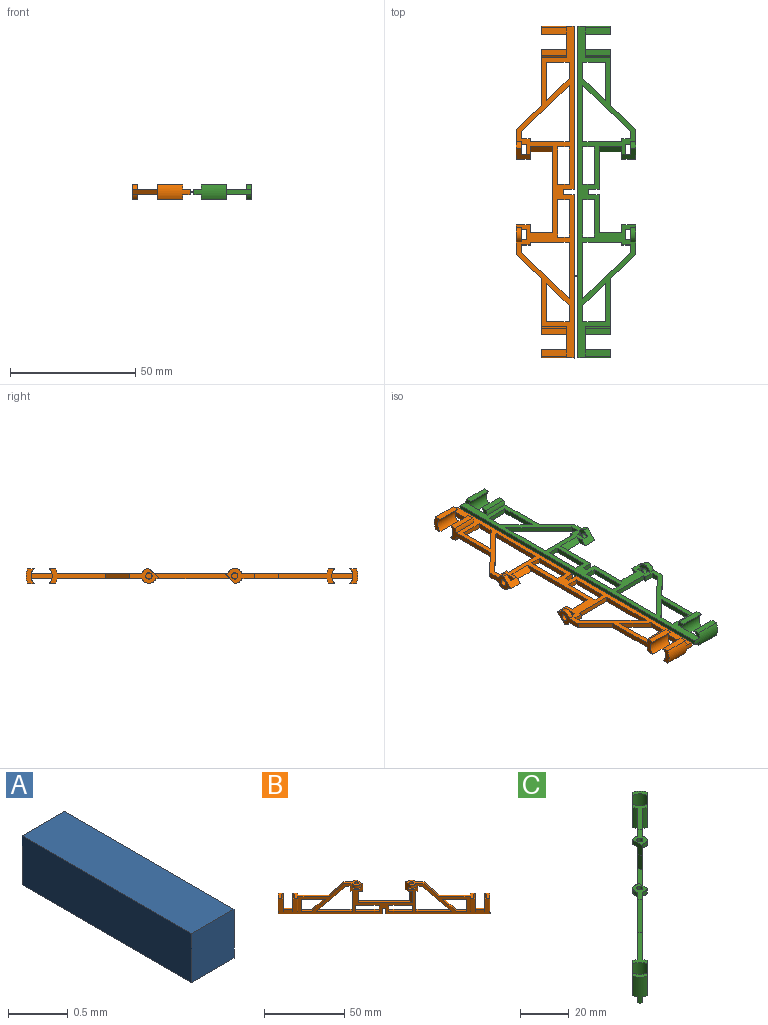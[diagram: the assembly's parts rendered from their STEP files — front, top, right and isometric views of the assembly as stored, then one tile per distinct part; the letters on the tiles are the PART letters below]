
ASSEMBLY  parts=3 mates=2
PART A: 6 faces, bbox 0.5x2x0.5 mm
  f0: plane 2x0.5mm, normal (0,0,-1), area 1mm2, adj f1,f3,f4,f5
  f1: plane 2x0.5mm, normal (1,0,0), area 1mm2, adj f0,f2,f4,f5
  f2: plane 2x0.5mm, normal (0,0,1), area 1mm2, adj f1,f3,f4,f5
  f3: plane 2x0.5mm, normal (-1,0,0), area 1mm2, adj f0,f2,f4,f5
  f4: plane 0.5x0.5mm, normal (0,-1,0), area 0.2mm2, adj f0,f1,f2,f3
  f5: plane 0.5x0.5mm, normal (0,1,0), area 0.2mm2, adj f0,f1,f2,f3
PART B: 92 faces, bbox 96.8x96.8x23 mm
  f0: plane 47.5x47.5mm, normal (0,0,-1), area 130.4mm2, adj f1,f2,f31,f89
  f1: plane 93.58x93.58mm, normal (-0.71,-0.71,0), area 733.5mm2, adj f0,f3,f4,f5,f6,f8,f9,f12
  f2: plane 93.58x93.58mm, normal (0.71,0.71,0), area 733.1mm2, adj f0,f3,f4,f5,f6,f8,f9,f13
  f3: plane 6x5.12mm, normal (0,0,-1), area 17.6mm2, adj f1,f2,f5,f49,f51,f58,f59,f60
  f4: plane 6x5.12mm, normal (0,0,-1), area 17.7mm2, adj f1,f2,f46,f52,f54,f55,f56,f57
  f5: plane 5.72x5.5mm, normal (1,0,0), area 21.1mm2, adj f1,f2,f3,f16,f47,f50,f51,f59
  f6: plane 9.8x8.38mm, normal (0,0,1), area 31.2mm2, adj f1,f2,f15,f46,f55,f56,f57
  f7: plane 5.99x5.99mm, normal (0,0,1), area 12.8mm2, adj f10,f13,f21,f25
  f8: plane 18.66x18.66mm, normal (0,0,1), area 51.2mm2, adj f1,f2,f11,f12,f15,f17,f18,f22
  f9: plane 47.5x47.5mm, normal (0,0,-1), area 130.4mm2, adj f1,f2,f13,f91
  f10: cylinder r=4.25mm len=10mm, axis (0,0,1), area 66.6mm2, adj f7,f14,f20,f21,f24,f25
  f11: cylinder r=4.25mm len=10mm, axis (0,0,1), area 66.6mm2, adj f8,f14,f18,f19,f22,f23
  f12: cylinder r=6.25mm len=10mm, axis (0,0,1), area 21.2mm2, adj f1,f8,f22,f23
  f13: cylinder r=6.25mm len=13mm, axis (0,0,1), area 68.6mm2, adj f1,f2,f7,f9,f20,f21,f24,f25
  f14: plane 7.26x7.26mm, normal (0,0,1), area 16.8mm2, adj f1,f2,f10,f11
  f15: plane 10x8.2mm, normal (0.51,-0.51,0.69), area 27.7mm2, adj f1,f2,f6,f8
  f16: plane 9.8x8.38mm, normal (0,0,1), area 31.1mm2, adj f1,f2,f5,f33,f58,f59,f60
  f17: cylinder r=6.25mm len=10mm, axis (0,0,1), area 21.2mm2, adj f2,f8,f18,f19
  f18: plane 10x1.75mm, normal (0.71,0.71,0), area 24.7mm2, adj f8,f11,f17,f19
  f19: plane 3.65x2.37mm, normal (0,0,-1), area 4.4mm2, adj f2,f11,f17,f18
  f20: plane 3.65x2.37mm, normal (0,0,-1), area 4.4mm2, adj f2,f10,f13,f21
  f21: plane 10x1.75mm, normal (0.71,0.71,0), area 24.7mm2, adj f7,f10,f13,f20
  f22: plane 10x1.75mm, normal (-0.71,-0.71,0), area 24.7mm2, adj f8,f11,f12,f23
  f23: plane 3.65x2.37mm, normal (0,0,-1), area 4.4mm2, adj f1,f11,f12,f22
  f24: plane 3.65x2.37mm, normal (0,0,-1), area 4.4mm2, adj f1,f10,f13,f25
  f25: plane 10x1.75mm, normal (-0.71,-0.71,0), area 24.7mm2, adj f7,f10,f13,f24
  f26: plane 5.99x5.99mm, normal (0,0,1), area 12.8mm2, adj f28,f31,f38,f42
  f27: plane 18.66x18.66mm, normal (0,0,1), area 51.2mm2, adj f1,f2,f29,f30,f33,f34,f35,f39
  f28: cylinder r=4.25mm len=10mm, axis (0,0,1), area 66.6mm2, adj f26,f32,f37,f38,f41,f42
  f29: cylinder r=4.25mm len=10mm, axis (0,0,1), area 66.6mm2, adj f27,f32,f35,f36,f39,f40
  f30: cylinder r=6.25mm len=10mm, axis (0,0,1), area 21.2mm2, adj f1,f27,f39,f40
  f31: cylinder r=6.25mm len=13mm, axis (0,0,1), area 68.6mm2, adj f0,f1,f2,f26,f37,f38,f41,f42
  f32: plane 7.26x7.26mm, normal (0,0,1), area 16.8mm2, adj f1,f2,f28,f29
  f33: plane 10x8.2mm, normal (-0.51,0.51,0.69), area 27.7mm2, adj f1,f2,f16,f27
  f34: cylinder r=6.25mm len=10mm, axis (0,0,1), area 21.2mm2, adj f2,f27,f35,f36
  f35: plane 10x1.75mm, normal (0.71,0.71,0), area 24.7mm2, adj f27,f29,f34,f36
  f36: plane 3.65x2.37mm, normal (0,0,-1), area 4.4mm2, adj f2,f29,f34,f35
  f37: plane 3.65x2.37mm, normal (0,0,-1), area 4.4mm2, adj f2,f28,f31,f38
  f38: plane 10x1.75mm, normal (0.71,0.71,0), area 24.7mm2, adj f26,f28,f31,f37
  f39: plane 10x1.75mm, normal (-0.71,-0.71,0), area 24.7mm2, adj f27,f29,f30,f40
  f40: plane 3.65x2.37mm, normal (0,0,-1), area 4.4mm2, adj f1,f29,f30,f39
  f41: plane 3.65x2.37mm, normal (0,0,-1), area 4.4mm2, adj f1,f28,f31,f42
  f42: plane 10x1.75mm, normal (-0.71,-0.71,0), area 24.7mm2, adj f26,f28,f31,f41
  f43: plane 26.83x24mm, normal (0,0,1), area 67.9mm2, adj f1,f2,f44,f48
  f44: plane 9x2.83mm, normal (-1,0,0), area 25.5mm2, adj f1,f2,f43,f45
  f45: plane 4.83x2mm, normal (0,0,-1), area 5.7mm2, adj f1,f2,f44,f46
  f46: plane 5.6x5.5mm, normal (-1,0,0), area 20.8mm2, adj f1,f2,f4,f6,f45,f53,f54,f57
  f47: plane 4.83x2mm, normal (0,0,-1), area 5.7mm2, adj f1,f2,f5,f48
  f48: plane 9x2.83mm, normal (1,0,0), area 25.5mm2, adj f1,f2,f43,f47
  f49: plane 2x1.41mm, normal (0.71,-0.71,0), area 4mm2, adj f1,f2,f3,f50
  f50: plane 4.31x4.25mm, normal (0,0,1), area 8.2mm2, adj f1,f2,f5,f49,f51
  f51: plane 2x1.35mm, normal (-0.71,0.71,0), area 3.8mm2, adj f1,f3,f5,f50
  f52: plane 2x1.41mm, normal (-0.71,0.71,0), area 4mm2, adj f1,f2,f4,f53
  f53: plane 4.31x4.25mm, normal (0,0,1), area 8.2mm2, adj f1,f2,f46,f52,f54
  f54: plane 2x1.35mm, normal (0.71,-0.71,0), area 3.8mm2, adj f2,f4,f46,f53
  f55: cylinder r=1.25mm len=2.5mm, axis (0,0,1), area 15.7mm2, adj f4,f6
  f56: cylinder r=3mm len=4.33mm, axis (0,0,1), area 14.9mm2, adj f2,f4,f6
  f57: cylinder r=3mm len=3.37mm, axis (0,0,1), area 7.3mm2, adj f1,f4,f6,f46
  f58: cylinder r=1.25mm len=2.5mm, axis (0,0,1), area 15.7mm2, adj f3,f16
  f59: cylinder r=3mm len=3.45mm, axis (0,0,1), area 7.5mm2, adj f2,f3,f5,f16
  f60: cylinder r=3mm len=4.25mm, axis (0,0,1), area 14.6mm2, adj f1,f3,f16
  f61: plane 3.53x3.53mm, normal (0,0,-1), area 6mm2, adj f1,f2,f62,f64
  f62: plane 3.5x1.41mm, normal (-0.71,0.71,0), area 7mm2, adj f1,f2,f61,f63
  f63: plane 2.25x2.25mm, normal (0,0,-1), area 2.4mm2, adj f1,f2,f62,f65
  f64: plane 19x14.31mm, normal (0.51,-0.51,-0.69), area 52.7mm2, adj f1,f2,f61,f66
  f65: plane 15.5x1.41mm, normal (-0.71,0.71,0), area 31mm2, adj f1,f2,f63,f66
  f66: plane 17.27x17.27mm, normal (0,0,1), area 44.8mm2, adj f1,f2,f64,f65
  f67: plane 4.5x1.41mm, normal (0.71,-0.71,0), area 9mm2, adj f1,f2,f68,f69
  f68: plane 12x12mm, normal (0,0,1), area 29.9mm2, adj f1,f2,f67,f70
  f69: plane 12x12mm, normal (0,0,-1), area 29.9mm2, adj f1,f2,f67,f70
  f70: plane 4.5x1.41mm, normal (-0.71,0.71,0), area 9mm2, adj f1,f2,f68,f69
  f71: plane 3.5x1.41mm, normal (0.71,-0.71,0), area 7mm2, adj f1,f2,f72,f76
  f72: plane 3.53x3.53mm, normal (0,0,-1), area 6mm2, adj f1,f2,f71,f73
  f73: plane 19x14.31mm, normal (-0.51,0.51,-0.69), area 52.7mm2, adj f1,f2,f72,f74
  f74: plane 17.27x17.27mm, normal (0,0,1), area 44.8mm2, adj f1,f2,f73,f75
  f75: plane 15.5x1.41mm, normal (0.71,-0.71,0), area 31mm2, adj f1,f2,f74,f76
  f76: plane 2.25x2.25mm, normal (0,0,-1), area 2.4mm2, adj f1,f2,f71,f75
  f77: plane 9x7.52mm, normal (-0.51,0.51,0.69), area 25mm2, adj f1,f2,f78,f79
  f78: plane 12.24x12.24mm, normal (0,0,-1), area 30.6mm2, adj f1,f2,f77,f80
  f79: plane 6.13x6.13mm, normal (0,0,1), area 13.3mm2, adj f1,f2,f77,f80
  f80: plane 9x1.41mm, normal (0.71,-0.71,0), area 18mm2, adj f1,f2,f78,f79
  f81: plane 9x1.41mm, normal (-0.71,0.71,0), area 18mm2, adj f1,f2,f82,f84
  f82: plane 6.13x6.13mm, normal (0,0,1), area 13.3mm2, adj f1,f2,f81,f83
  f83: plane 9x7.52mm, normal (0.51,-0.51,0.69), area 25mm2, adj f1,f2,f82,f84
  f84: plane 12.24x12.24mm, normal (0,0,-1), area 30.6mm2, adj f1,f2,f81,f83
  f85: plane 12x12mm, normal (0,0,1), area 29.9mm2, adj f1,f2,f86,f88
  f86: plane 4.5x1.41mm, normal (0.71,-0.71,0), area 9mm2, adj f1,f2,f85,f87
  f87: plane 12x12mm, normal (0,0,-1), area 29.9mm2, adj f1,f2,f86,f88
  f88: plane 4.5x1.41mm, normal (-0.71,0.71,0), area 9mm2, adj f1,f2,f85,f87
  f89: plane 4.25x1.41mm, normal (0.71,-0.71,0), area 8.5mm2, adj f0,f1,f2,f90
  f90: plane 2.83x2.83mm, normal (0,0,-1), area 4mm2, adj f1,f2,f89,f91
  f91: plane 4.25x1.41mm, normal (-0.71,0.71,0), area 8.5mm2, adj f1,f2,f9,f90
PART C: 92 faces, bbox 96.8x96.8x23 mm
  f0: plane 13.41x12mm, normal (0,0,1), area 31.9mm2, adj f1,f4,f44,f90
  f1: plane 93.58x93.58mm, normal (-0.71,0.71,0), area 733.1mm2, adj f0,f2,f3,f5,f6,f8,f9,f13
  f2: plane 6x5.12mm, normal (0,0,-1), area 17.6mm2, adj f1,f4,f5,f49,f51,f58,f59,f60
  f3: plane 6x5.12mm, normal (0,0,-1), area 17.7mm2, adj f1,f4,f46,f52,f54,f55,f56,f57
  f4: plane 93.58x93.58mm, normal (0.71,-0.71,0), area 733.5mm2, adj f0,f2,f3,f5,f6,f8,f9,f12
  f5: plane 5.72x5.5mm, normal (-1,0,0), area 21.1mm2, adj f1,f2,f4,f16,f47,f50,f51,f59
  f6: plane 9.8x8.38mm, normal (0,0,1), area 31.2mm2, adj f1,f4,f15,f46,f55,f56,f57
  f7: plane 5.99x5.99mm, normal (0,0,1), area 12.8mm2, adj f10,f13,f21,f25
  f8: plane 18.66x18.66mm, normal (0,0,1), area 51.2mm2, adj f1,f4,f11,f12,f15,f17,f18,f22
  f9: plane 94.99x94.99mm, normal (0,0,-1), area 264.9mm2, adj f1,f4,f13,f31
  f10: cylinder r=4.25mm len=10mm, axis (0,0,1), area 66.6mm2, adj f7,f14,f20,f21,f24,f25
  f11: cylinder r=4.25mm len=10mm, axis (0,0,1), area 66.6mm2, adj f8,f14,f18,f19,f22,f23
  f12: cylinder r=6.25mm len=10mm, axis (0,0,1), area 21.2mm2, adj f4,f8,f22,f23
  f13: cylinder r=6.25mm len=13mm, axis (0,0,1), area 68.6mm2, adj f1,f4,f7,f9,f20,f21,f24,f25
  f14: plane 7.26x7.26mm, normal (0,0,1), area 16.8mm2, adj f1,f4,f10,f11
  f15: plane 10x8.2mm, normal (-0.51,-0.51,0.69), area 27.7mm2, adj f1,f4,f6,f8
  f16: plane 9.8x8.38mm, normal (0,0,1), area 31.1mm2, adj f1,f4,f5,f33,f58,f59,f60
  f17: cylinder r=6.25mm len=10mm, axis (0,0,1), area 21.2mm2, adj f1,f8,f18,f19
  f18: plane 10x1.75mm, normal (-0.71,0.71,0), area 24.7mm2, adj f8,f11,f17,f19
  f19: plane 3.65x2.37mm, normal (0,0,-1), area 4.4mm2, adj f1,f11,f17,f18
  f20: plane 3.65x2.37mm, normal (0,0,-1), area 4.4mm2, adj f1,f10,f13,f21
  f21: plane 10x1.75mm, normal (-0.71,0.71,0), area 24.7mm2, adj f7,f10,f13,f20
  f22: plane 10x1.75mm, normal (0.71,-0.71,0), area 24.7mm2, adj f8,f11,f12,f23
  f23: plane 3.65x2.37mm, normal (0,0,-1), area 4.4mm2, adj f4,f11,f12,f22
  f24: plane 3.65x2.37mm, normal (0,0,-1), area 4.4mm2, adj f4,f10,f13,f25
  f25: plane 10x1.75mm, normal (0.71,-0.71,0), area 24.7mm2, adj f7,f10,f13,f24
  f26: plane 5.99x5.99mm, normal (0,0,1), area 12.8mm2, adj f28,f31,f38,f42
  f27: plane 18.66x18.66mm, normal (0,0,1), area 51.2mm2, adj f1,f4,f29,f30,f33,f34,f35,f39
  f28: cylinder r=4.25mm len=10mm, axis (0,0,1), area 66.6mm2, adj f26,f32,f37,f38,f41,f42
  f29: cylinder r=4.25mm len=10mm, axis (0,0,1), area 66.6mm2, adj f27,f32,f35,f36,f39,f40
  f30: cylinder r=6.25mm len=10mm, axis (0,0,1), area 21.2mm2, adj f4,f27,f39,f40
  f31: cylinder r=6.25mm len=13mm, axis (0,0,1), area 68.6mm2, adj f1,f4,f9,f26,f37,f38,f41,f42
  f32: plane 7.26x7.26mm, normal (0,0,1), area 16.8mm2, adj f1,f4,f28,f29
  f33: plane 10x8.2mm, normal (0.51,0.51,0.69), area 27.7mm2, adj f1,f4,f16,f27
  f34: cylinder r=6.25mm len=10mm, axis (0,0,1), area 21.2mm2, adj f1,f27,f35,f36
  f35: plane 10x1.75mm, normal (-0.71,0.71,0), area 24.7mm2, adj f27,f29,f34,f36
  f36: plane 3.65x2.37mm, normal (0,0,-1), area 4.4mm2, adj f1,f29,f34,f35
  f37: plane 3.65x2.37mm, normal (0,0,-1), area 4.4mm2, adj f1,f28,f31,f38
  f38: plane 10x1.75mm, normal (-0.71,0.71,0), area 24.7mm2, adj f26,f28,f31,f37
  f39: plane 10x1.75mm, normal (0.71,-0.71,0), area 24.7mm2, adj f27,f29,f30,f40
  f40: plane 3.65x2.37mm, normal (0,0,-1), area 4.4mm2, adj f4,f29,f30,f39
  f41: plane 3.65x2.37mm, normal (0,0,-1), area 4.4mm2, adj f4,f28,f31,f42
  f42: plane 10x1.75mm, normal (0.71,-0.71,0), area 24.7mm2, adj f26,f28,f31,f41
  f43: plane 13.41x12mm, normal (0,0,1), area 31.9mm2, adj f1,f4,f48,f89
  f44: plane 9x2.83mm, normal (1,0,0), area 25.5mm2, adj f0,f1,f4,f45
  f45: plane 4.83x2mm, normal (0,0,-1), area 5.7mm2, adj f1,f4,f44,f46
  f46: plane 5.6x5.5mm, normal (1,0,0), area 20.8mm2, adj f1,f3,f4,f6,f45,f53,f54,f57
  f47: plane 4.83x2mm, normal (0,0,-1), area 5.7mm2, adj f1,f4,f5,f48
  f48: plane 9x2.83mm, normal (-1,0,0), area 25.5mm2, adj f1,f4,f43,f47
  f49: plane 2x1.41mm, normal (-0.71,-0.71,0), area 4mm2, adj f1,f2,f4,f50
  f50: plane 4.31x4.25mm, normal (0,0,1), area 8.2mm2, adj f1,f4,f5,f49,f51
  f51: plane 2x1.35mm, normal (0.71,0.71,0), area 3.8mm2, adj f2,f4,f5,f50
  f52: plane 2x1.41mm, normal (0.71,0.71,0), area 4mm2, adj f1,f3,f4,f53
  f53: plane 4.31x4.25mm, normal (0,0,1), area 8.2mm2, adj f1,f4,f46,f52,f54
  f54: plane 2x1.35mm, normal (-0.71,-0.71,0), area 3.8mm2, adj f1,f3,f46,f53
  f55: cylinder r=1.25mm len=2.5mm, axis (0,0,1), area 15.7mm2, adj f3,f6
  f56: cylinder r=3mm len=4.33mm, axis (0,0,1), area 14.9mm2, adj f1,f3,f6
  f57: cylinder r=3mm len=3.37mm, axis (0,0,1), area 7.3mm2, adj f3,f4,f6,f46
  f58: cylinder r=1.25mm len=2.5mm, axis (0,0,1), area 15.7mm2, adj f2,f16
  f59: cylinder r=3mm len=3.45mm, axis (0,0,1), area 7.5mm2, adj f1,f2,f5,f16
  f60: cylinder r=3mm len=4.25mm, axis (0,0,1), area 14.6mm2, adj f2,f4,f16
  f61: plane 3.53x3.53mm, normal (0,0,-1), area 6mm2, adj f1,f4,f62,f64
  f62: plane 3.5x1.41mm, normal (0.71,0.71,0), area 7mm2, adj f1,f4,f61,f63
  f63: plane 2.25x2.25mm, normal (0,0,-1), area 2.4mm2, adj f1,f4,f62,f65
  f64: plane 19x14.31mm, normal (-0.51,-0.51,-0.69), area 52.7mm2, adj f1,f4,f61,f66
  f65: plane 15.5x1.41mm, normal (0.71,0.71,0), area 31mm2, adj f1,f4,f63,f66
  f66: plane 17.27x17.27mm, normal (0,0,1), area 44.8mm2, adj f1,f4,f64,f65
  f67: plane 4.5x1.41mm, normal (-0.71,-0.71,0), area 9mm2, adj f1,f4,f68,f69
  f68: plane 12x12mm, normal (0,0,1), area 29.9mm2, adj f1,f4,f67,f70
  f69: plane 12x12mm, normal (0,0,-1), area 29.9mm2, adj f1,f4,f67,f70
  f70: plane 4.5x1.41mm, normal (0.71,0.71,0), area 9mm2, adj f1,f4,f68,f69
  f71: plane 3.5x1.41mm, normal (-0.71,-0.71,0), area 7mm2, adj f1,f4,f72,f76
  f72: plane 3.53x3.53mm, normal (0,0,-1), area 6mm2, adj f1,f4,f71,f73
  f73: plane 19x14.31mm, normal (0.51,0.51,-0.69), area 52.7mm2, adj f1,f4,f72,f74
  f74: plane 17.27x17.27mm, normal (0,0,1), area 44.8mm2, adj f1,f4,f73,f75
  f75: plane 15.5x1.41mm, normal (-0.71,-0.71,0), area 31mm2, adj f1,f4,f74,f76
  f76: plane 2.25x2.25mm, normal (0,0,-1), area 2.4mm2, adj f1,f4,f71,f75
  f77: plane 9x7.52mm, normal (0.51,0.51,0.69), area 25mm2, adj f1,f4,f78,f79
  f78: plane 12.24x12.24mm, normal (0,0,-1), area 30.6mm2, adj f1,f4,f77,f80
  f79: plane 6.13x6.13mm, normal (0,0,1), area 13.3mm2, adj f1,f4,f77,f80
  f80: plane 9x1.41mm, normal (-0.71,-0.71,0), area 18mm2, adj f1,f4,f78,f79
  f81: plane 9x1.41mm, normal (0.71,0.71,0), area 18mm2, adj f1,f4,f82,f84
  f82: plane 6.13x6.13mm, normal (0,0,1), area 13.3mm2, adj f1,f4,f81,f83
  f83: plane 9x7.52mm, normal (-0.51,-0.51,0.69), area 25mm2, adj f1,f4,f82,f84
  f84: plane 12.24x12.24mm, normal (0,0,-1), area 30.6mm2, adj f1,f4,f81,f83
  f85: plane 12x12mm, normal (0,0,1), area 29.9mm2, adj f1,f4,f86,f88
  f86: plane 4.5x1.41mm, normal (-0.71,-0.71,0), area 9mm2, adj f1,f4,f85,f87
  f87: plane 12x12mm, normal (0,0,-1), area 29.9mm2, adj f1,f4,f86,f88
  f88: plane 4.5x1.41mm, normal (0.71,0.71,0), area 9mm2, adj f1,f4,f85,f87
  f89: plane 4.25x1.41mm, normal (-0.71,-0.71,0), area 8.5mm2, adj f1,f4,f43,f91
  f90: plane 4.25x1.41mm, normal (0.71,0.71,0), area 8.5mm2, adj f0,f1,f4,f91
  f91: plane 2.83x2.83mm, normal (0,0,1), area 4mm2, adj f1,f4,f89,f90
PLACE A rot(axis=(0,0,1),90deg) t=(-0.96,-0.23,0.49)mm
PLACE B rot(axis=(0.36,-0.86,-0.36),98.4deg) t=(-24.96,33.38,0.49)mm
PLACE C rot(axis=(0.36,0.86,0.36),98.4deg) t=(22.54,-65.61,99.48)mm
MATE fastened B.f9 <-> A.f5  axis (1,0,0) through (-1.96,-0.23,0.49)mm
MATE fastened C.f89 <-> B.f89  axis (0,-1,0) through (5.91,34.38,0.49)mm
